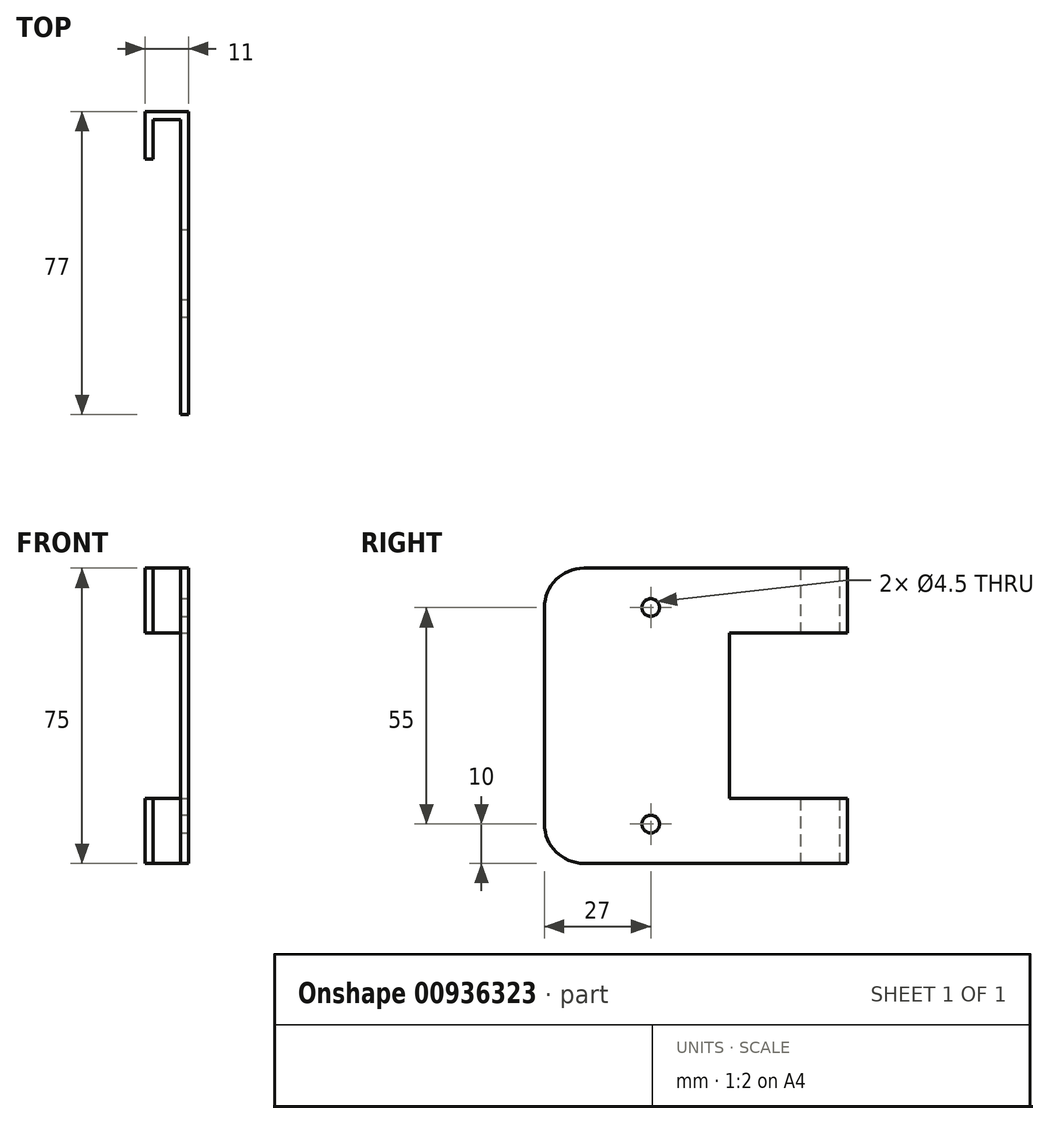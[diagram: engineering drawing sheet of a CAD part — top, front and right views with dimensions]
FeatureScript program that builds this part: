
annotation { "Feature Type Name" : "Feature", "Feature Type Description" : "" }
export const myFeature = defineFeature(function(context is Context, id is Id, definition is map)
    precondition{}
    {
        {
            assignVariable(context, id + "F0", {"name" : "hole", "anyValue" : 4.5});
        }
        {
            assignVariable(context, id + "F1", {"name" : "wh", "anyValue" : 75});
        }
        {
            var Q0;
            Q0=qCreatedBy(makeId("Top.planeOp"),FACE);
            var sketch = newSketch(context, id + "F2", { "sketchPlane" : qUnion([Q0])});
            skLineSegment(sketch, "E0", {"start": v(2, 0) * mm, "end": v(0, 0) * mm});
            skLineSegment(sketch, "E1", {"start": v(0, 0) * mm, "end": v(0, 12) * mm});
            skLineSegment(sketch, "E2", {"start": v(0, 12) * mm, "end": v(11, 12) * mm});
            skLineSegment(sketch, "E3", {"start": v(11, 12) * mm, "end": v(11, -65) * mm});
            skLineSegment(sketch, "E4", {"start": v(11, -65) * mm, "end": v(9, -65) * mm});
            skLineSegment(sketch, "E5", {"start": v(9, -65) * mm, "end": v(9, 10) * mm});
            skLineSegment(sketch, "E6", {"start": v(2, 0) * mm, "end": v(2, 10) * mm});
            skLineSegment(sketch, "E7", {"start": v(2, 10) * mm, "end": v(9, 10) * mm});
            skSolve(sketch);
        }
        {
            var Q0;
            Q0 = qSketchRegion(id + "F2", true);
            extrude(context, id + "F3", {"entities" : qUnion([Q0]), "depth" : (getVariable(context, 'wh')) * mm, "offsetDistance" : 25 * mm});
        }
        {
            var Q0;
            Q0=makeQuery(id+"F3.opExtrude","SWEPT_FACE",FACE,{"disambiguationData":[OSD([sQuery(id+"F2.wireOp",EDGE,"E3")])]});
            var sketch = newSketch(context, id + "F4", { "sketchPlane" : qUnion([Q0])});
            skLineSegment(sketch, "E8", {"start": v(-65, 37.5) * mm, "end": v(12, 37.5) * mm, "construction": true});
            skLineSegment(sketch, "E9.bottom", {"start": v(12, 58.5) * mm, "end": v(-18, 58.5) * mm});
            skLineSegment(sketch, "E9.top", {"start": v(12, 16.5) * mm, "end": v(-18, 16.5) * mm});
            skLineSegment(sketch, "E9.left", {"start": v(12, 58.5) * mm, "end": v(12, 16.5) * mm});
            skLineSegment(sketch, "E9.right", {"start": v(-18, 58.5) * mm, "end": v(-18, 16.5) * mm});
            skLineSegment(sketch, "E10", {"start": v(-38, 75) * mm, "end": v(-38, 0) * mm, "construction": true});
            skPoint(sketch, "E11", {"position": v(-38, 65) * mm});
            skPoint(sketch, "E12", {"position": v(-38, 10) * mm});
            skSolve(sketch);
        }
        {
            var Q0;
            Q0=makeQuery(id+"F4.imprint","IMPRINT",FACE,{"disambiguationData":[TD([[makeQuery(id+"F4.imprint","IMPRINT",EDGE,{"derivedFrom":sQuery(id+"F4.wireOp",EDGE,"E9.bottom")}),1.0]])]});
            extrude(context, id + "F5", {"entities" : qUnion([Q0]), "operationType" : NewBodyOperationType.REMOVE, "oppositeDirection" : true, "depth" : 25 * mm, "offsetDistance" : 25 * mm});
        }
        {
            var Q0;
            Q0=sQuery(id+"F4.wireOp",VERTEX,"E11");
            var Q1;
            Q1=sQuery(id+"F4.wireOp",VERTEX,"E12");
            var Q2;
            Q2=makeQuery(id+"F3.opExtrude","SWEPT_BODY",BODY,{"disambiguationData":[OSD([sQuery(id+"F2.wireOp",EDGE,"E0"),sQuery(id+"F2.wireOp",EDGE,"E1"),sQuery(id+"F2.wireOp",EDGE,"E2"),sQuery(id+"F2.wireOp",EDGE,"E3"),sQuery(id+"F2.wireOp",EDGE,"E4"),sQuery(id+"F2.wireOp",EDGE,"E5"),sQuery(id+"F2.wireOp",EDGE,"E6"),sQuery(id+"F2.wireOp",EDGE,"E7")])]});
            hole(context, id + "F6", {"style" : HoleStyle.SIMPLE, "endStyle" : HoleEndStyle.THROUGH, "holeDiameter" : (getVariable(context, 'hole')) * mm, "majorDiameter" : 5 * mm, "isTappedThrough" : true, "tappedDepth" : 12 * mm, "tapClearance" : 3, "locations" : qUnion([Q0, Q1]), "scope" : qUnion([Q2])});
        }
        {
            var Q0;
            Q0=makeQuery(id+"F3.opExtrude","CAP_EDGE",EDGE,{"disambiguationData":[OSD([sQuery(id+"F2.wireOp",EDGE,"E4")])],"isStart":true});
            var Q1;
            Q1=makeQuery(id+"F3.opExtrude","CAP_EDGE",EDGE,{"disambiguationData":[OSD([sQuery(id+"F2.wireOp",EDGE,"E4")])],"isStart":false});
            fillet(context, id + "F7", {"entities" : qUnion([Q0, Q1]), "radius" : 10 * mm, "tangentPropagation" : true, "allowEdgeOverflow" : false});
        }
    });
